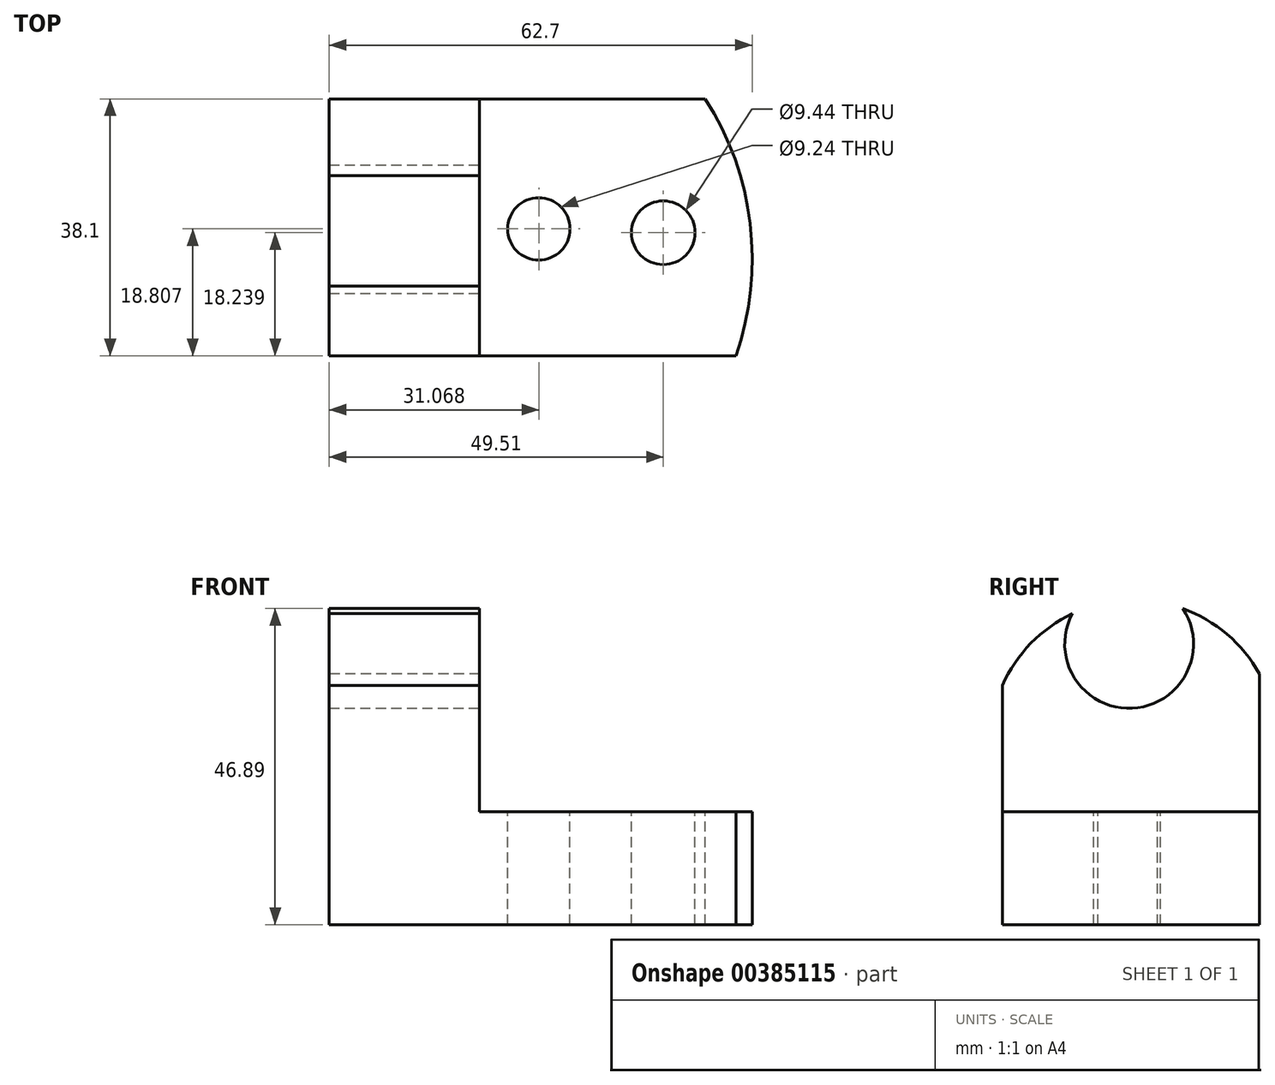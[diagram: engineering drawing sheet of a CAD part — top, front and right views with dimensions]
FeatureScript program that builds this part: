
annotation { "Feature Type Name" : "Feature", "Feature Type Description" : "" }
export const myFeature = defineFeature(function(context is Context, id is Id, definition is map)
    precondition{}
    {
        {
            var Q0;
            Q0=qCreatedBy(makeId("Front.planeOp"),FACE);
            var sketch = newSketch(context, id + "F0", { "sketchPlane" : qUnion([Q0])});
            skLineSegment(sketch, "E0", {"start": v(0, 0) * mm, "end": v(0, 49.37) * mm});
            skLineSegment(sketch, "E1", {"start": v(0, 49.37) * mm, "end": v(22.27, 49.37) * mm});
            skLineSegment(sketch, "E2", {"start": v(22.27, 49.37) * mm, "end": v(22.27, 16.74) * mm});
            skLineSegment(sketch, "E3", {"start": v(22.27, 16.74) * mm, "end": v(68.8, 16.74) * mm});
            skLineSegment(sketch, "E4", {"start": v(68.8, 16.74) * mm, "end": v(68.8, 0) * mm});
            skLineSegment(sketch, "E5", {"start": v(68.8, 0) * mm, "end": v(0, 0) * mm});
            skSolve(sketch);
        }
        {
            var Q0;
            Q0 = qSketchRegion(id + "F0", true);
            extrude(context, id + "F1", {"entities" : qUnion([Q0]), "depth" : 38.1 * mm});
        }
        {
            var Q0;
            Q0=makeQuery(id+"F1.opExtrude","SWEPT_FACE",FACE,{"disambiguationData":[OSD([sQuery(id+"F0.wireOp",EDGE,"E3")])]});
            var sketch = newSketch(context, id + "F2", { "sketchPlane" : qUnion([Q0])});
            skArc(sketch, "E6", {"start": v(60.3, -38.1) * mm, "mid": v(66.45, -18.05) * mm, "end": v(55.75, 0) * mm});
            skSolve(sketch);
        }
        {
            var Q0;
            {var subQ0=sQuery(id+"F2.wireOp",EDGE,"E6");Q0=makeQuery(id+"F2.imprint","IMPRINT",FACE,{"disambiguationData":[TD([[makeQuery(id+"F2.imprint","IMPRINT",EDGE,{"derivedFrom":subQ0}),-1.0]])]});}
            extrude(context, id + "F3", {"entities" : qUnion([Q0]), "operationType" : NewBodyOperationType.REMOVE, "oppositeDirection" : true, "depth" : 25.4 * mm});
        }
        {
            var Q0;
            Q0=makeQuery(id+"F1.opExtrude","SWEPT_FACE",FACE,{"disambiguationData":[OSD([sQuery(id+"F0.wireOp",EDGE,"E3")])]});
            var sketch = newSketch(context, id + "F4", { "sketchPlane" : qUnion([Q0])});
            skCircle(sketch, "E7", {"center": v(31.07, -19.3) * mm, "radius": 4.62 * mm});
            skCircle(sketch, "E8", {"center": v(49.5, -19.86) * mm, "radius": 4.72 * mm});
            skSolve(sketch);
        }
        {
            var Q0;
            Q0=makeQuery(id+"F4.imprint","IMPRINT",FACE,{"disambiguationData":[TD([[makeQuery(id+"F4.imprint","IMPRINT",EDGE,{"derivedFrom":sQuery(id+"F4.wireOp",EDGE,"E7")}),1.0]])]});
            var Q1;
            Q1=makeQuery(id+"F4.imprint","IMPRINT",FACE,{"disambiguationData":[TD([[makeQuery(id+"F4.imprint","IMPRINT",EDGE,{"derivedFrom":sQuery(id+"F4.wireOp",EDGE,"E8")}),1.0]])]});
            extrude(context, id + "F5", {"entities" : qUnion([Q0, Q1]), "operationType" : NewBodyOperationType.REMOVE, "oppositeDirection" : true, "depth" : 25.4 * mm});
        }
        {
            var Q0;
            Q0=makeQuery(id+"F1.opExtrude","SWEPT_FACE",FACE,{"disambiguationData":[OSD([sQuery(id+"F0.wireOp",EDGE,"E0")])]});
            var sketch = newSketch(context, id + "F6", { "sketchPlane" : qUnion([Q0])});
            skArc(sketch, "E9", {"start": v(38.1, 35.47) * mm, "mid": v(19.58, 48.15) * mm, "end": v(0, 37.17) * mm});
            skSolve(sketch);
        }
        {
            var Q0;
            {var subQ0=sQuery(id+"F6.wireOp",EDGE,"E9");Q0=makeQuery(id+"F6.imprint","IMPRINT",FACE,{"disambiguationData":[TD([[makeQuery(id+"F6.imprint","IMPRINT",EDGE,{"derivedFrom":subQ0}),-1.0]])]});}
            extrude(context, id + "F7", {"entities" : qUnion([Q0]), "operationType" : NewBodyOperationType.REMOVE, "oppositeDirection" : true, "depth" : 25.4 * mm});
        }
        {
            var Q0;
            Q0=makeQuery(id+"F1.opExtrude","SWEPT_FACE",FACE,{"disambiguationData":[OSD([sQuery(id+"F0.wireOp",EDGE,"E2")])]});
            var sketch = newSketch(context, id + "F8", { "sketchPlane" : qUnion([Q0])});
            skArc(sketch, "E10", {"start": v(-27.74, 46.12) * mm, "mid": v(-18.87, 32.09) * mm, "end": v(-11.37, 46.9) * mm});
            skSolve(sketch);
        }
        {
            var Q0;
            {var subQ0=sQuery(id+"F8.wireOp",EDGE,"E10");Q0=makeQuery(id+"F8.imprint","IMPRINT",FACE,{"disambiguationData":[TD([[makeQuery(id+"F8.imprint","IMPRINT",EDGE,{"derivedFrom":subQ0}),1.0]])]});}
            extrude(context, id + "F9", {"entities" : qUnion([Q0]), "operationType" : NewBodyOperationType.REMOVE, "oppositeDirection" : true, "depth" : 25.4 * mm});
        }
        {
            var Q0;
            Q0=makeQuery(id+"F1.opExtrude","SWEPT_FACE",FACE,{"disambiguationData":[OSD([sQuery(id+"F0.wireOp",EDGE,"E3")])]});
            var sketch = newSketch(context, id + "F10", { "sketchPlane" : qUnion([Q0])});
            skArc(sketch, "E11", {"start": v(60.3, -38.1) * mm, "mid": v(62.4, -18.53) * mm, "end": v(55.75, 0) * mm});
            skSolve(sketch);
        }
        {
            var Q0;
            Q0=makeQuery(id+"F10.imprint","IMPRINT",FACE,{"disambiguationData":[TD([[makeQuery(id+"F10.imprint","IMPRINT",EDGE,{"derivedFrom":sQuery(id+"F10.wireOp",EDGE,"E11")}),-1.0]])]});
            extrude(context, id + "F11", {"entities" : qUnion([Q0]), "operationType" : NewBodyOperationType.REMOVE, "oppositeDirection" : true, "depth" : 25.4 * mm});
        }
    });
